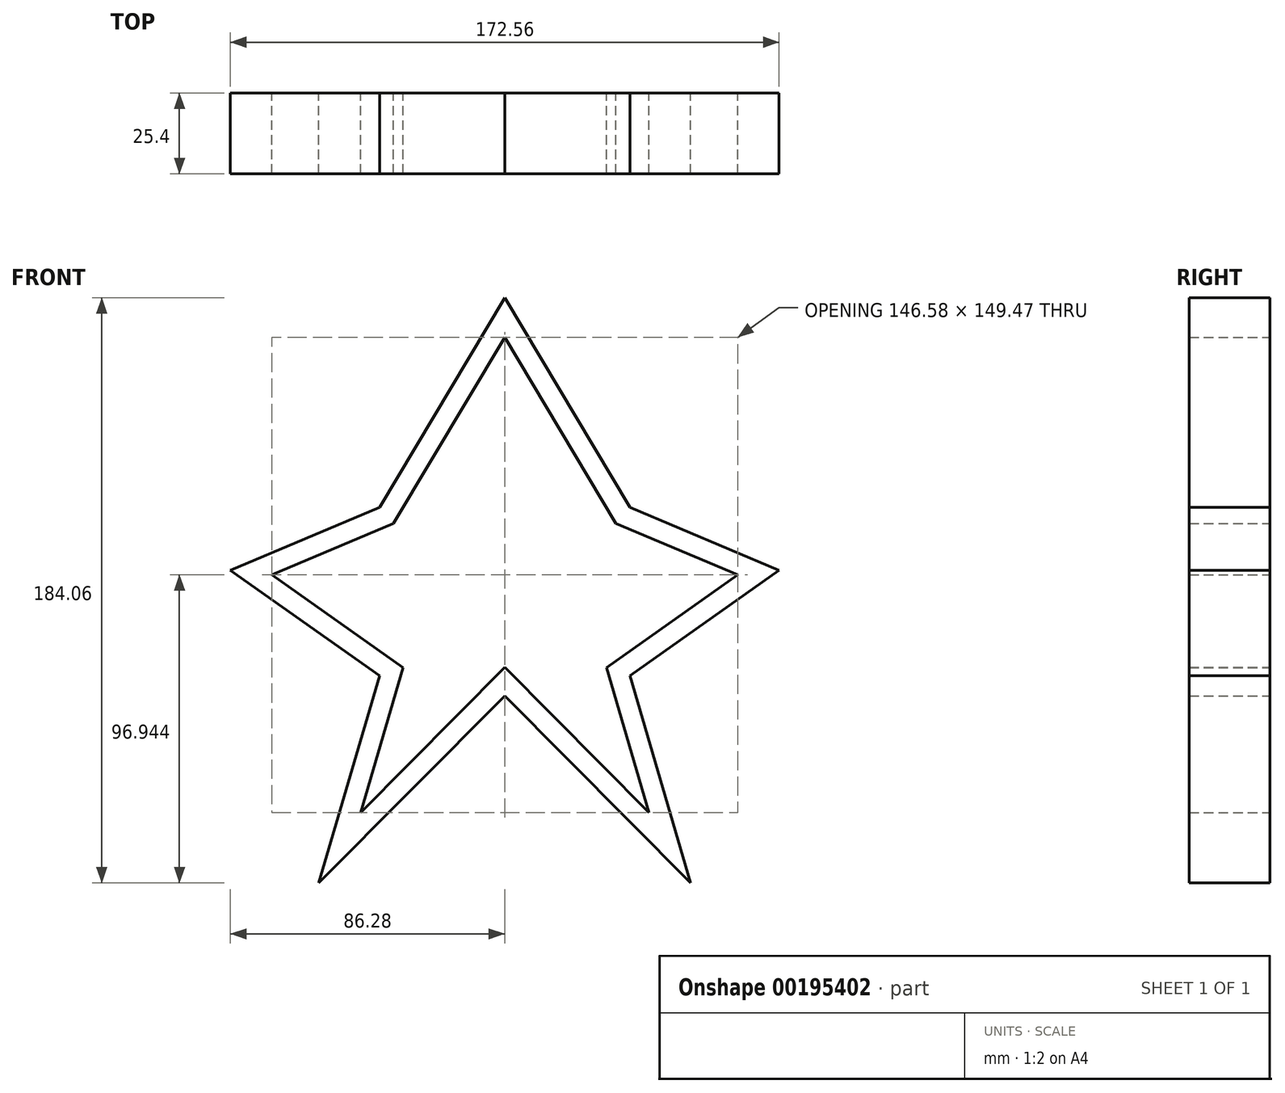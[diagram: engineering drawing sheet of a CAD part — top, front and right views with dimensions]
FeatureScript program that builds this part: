
annotation { "Feature Type Name" : "Feature", "Feature Type Description" : "" }
export const myFeature = defineFeature(function(context is Context, id is Id, definition is map)
    precondition{}
    {
        {
            var Q0;
            Q0=qCreatedBy(makeId("Front.planeOp"),FACE);
            var sketch = newSketch(context, id + "F0", { "sketchPlane" : qUnion([Q0])});
            skLineSegment(sketch, "E0", {"start": v(0, 85.67) * mm, "end": v(-39.39, 19.75) * mm});
            skLineSegment(sketch, "E1", {"start": v(-39.39, 19.75) * mm, "end": v(-86.28, 0) * mm});
            skLineSegment(sketch, "E2", {"start": v(-86.28, 0) * mm, "end": v(-39.39, -33.2) * mm});
            skLineSegment(sketch, "E3", {"start": v(-39.39, -33.2) * mm, "end": v(-58.5, -98.4) * mm});
            skLineSegment(sketch, "E4", {"start": v(-58.5, -98.4) * mm, "end": v(0, -39.55) * mm});
            skLineSegment(sketch, "E5", {"start": v(0, 85.67) * mm, "end": v(0, -39.55) * mm, "construction": true});
            skLineSegment(sketch, "E6.MirrorCS", {"start": v(0, 85.67) * mm, "end": v(39.39, 19.75) * mm});
            skLineSegment(sketch, "E7.MirrorCS", {"start": v(39.39, 19.75) * mm, "end": v(86.28, 0) * mm});
            skLineSegment(sketch, "E8.MirrorCS", {"start": v(86.28, 0) * mm, "end": v(39.39, -33.2) * mm});
            skLineSegment(sketch, "E9.MirrorCS", {"start": v(39.39, -33.2) * mm, "end": v(58.5, -98.4) * mm});
            skLineSegment(sketch, "E10.MirrorCS", {"start": v(58.5, -98.4) * mm, "end": v(0, -39.55) * mm});
            skSolve(sketch);
        }
        {
            var Q0;
            Q0=qCreatedBy(makeId("Front.planeOp"),FACE);
            var sketch = newSketch(context, id + "F1", { "sketchPlane" : qUnion([Q0])});
            skLineSegment(sketch, "E11.0", {"start": v(73.3, -1.42) * mm, "end": v(35, 14.7) * mm});
            skLineSegment(sketch, "E11.1", {"start": v(32.02, -30.64) * mm, "end": v(73.3, -1.42) * mm});
            skLineSegment(sketch, "E11.2", {"start": v(35, 14.7) * mm, "end": v(0, 73.29) * mm});
            skLineSegment(sketch, "E11.3", {"start": v(45.37, -76.18) * mm, "end": v(32.02, -30.64) * mm});
            skLineSegment(sketch, "E11.4", {"start": v(0, -30.55) * mm, "end": v(45.37, -76.18) * mm});
            skLineSegment(sketch, "E11.5", {"start": v(-45.37, -76.18) * mm, "end": v(0, -30.55) * mm});
            skLineSegment(sketch, "E11.6", {"start": v(0, 73.29) * mm, "end": v(-35, 14.7) * mm});
            skLineSegment(sketch, "E11.7", {"start": v(-35, 14.7) * mm, "end": v(-73.3, -1.42) * mm});
            skLineSegment(sketch, "E11.8", {"start": v(-73.3, -1.42) * mm, "end": v(-32.02, -30.64) * mm});
            skLineSegment(sketch, "E11.9", {"start": v(-32.02, -30.64) * mm, "end": v(-45.37, -76.18) * mm});
            skSolve(sketch);
        }
        {
            var Q0;
            Q0=makeQuery(id+"F0.imprint","IMPRINT",FACE,{"disambiguationData":[TD([[makeQuery(id+"F0.imprint","IMPRINT",EDGE,{"derivedFrom":sQuery(id+"F0.wireOp",EDGE,"E0")}),1.0]])]});
            extrude(context, id + "F2", {"entities" : qUnion([Q0]), "depth" : 25.4 * mm});
        }
        {
            var Q0;
            Q0=makeQuery(id+"F1.imprint","IMPRINT",FACE,{"disambiguationData":[TD([[makeQuery(id+"F1.imprint","IMPRINT",EDGE,{"derivedFrom":sQuery(id+"F1.wireOp",EDGE,"E11.0")}),1.0]])]});
            extrude(context, id + "F3", {"entities" : qUnion([Q0]), "operationType" : NewBodyOperationType.REMOVE, "depth" : 61.64 * mm});
        }
    });
